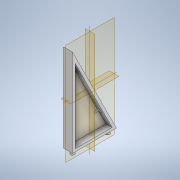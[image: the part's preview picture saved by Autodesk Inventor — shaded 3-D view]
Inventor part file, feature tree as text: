
AUTODESK INVENTOR PART (.ipt)
format: ipt  version: 2022.4 (Build 264492010, 492A)  size: 146,944 bytes
history: native  units: mm
features: extrude x4, sketch x4, mirror x1
ambient origin geometry x8: Origin, YZ Plane, XZ Plane, XY Plane, X Axis, Y Axis, Z Axis, Center Point
bodies: Solid1 (feature_tree)
feature tree (9):
  extrude  "Extrusion1"  Depth=100.0mm
  extrude  "Extrusion2"  Depth=3.0mm
  extrude  "Extrusion3"  Depth=5.0mm
  extrude  "Extrusion4"  Depth=10.0mm
  mirror  "Mirror1"
  sketch  "Sketch2"  dims[d0=50.0mm d1=100.0mm]
  sketch  "Sketch4"  dims[d2=10.0mm d3=0.0mm d8=3.0mm]
  sketch  "Sketch5"  dims[d9=7.0mm d10=0.0mm d11=5.0mm]
  sketch  "Sketch8"  dims[d12=5.0mm d13=20.0mm d15=40.0mm d16=10.0mm d18=10.0mm d20=5.0mm d21=0.0mm d31=111.803399mm d32=5.0mm d34=30.0mm d35=7.0mm d36=0.0mm]
